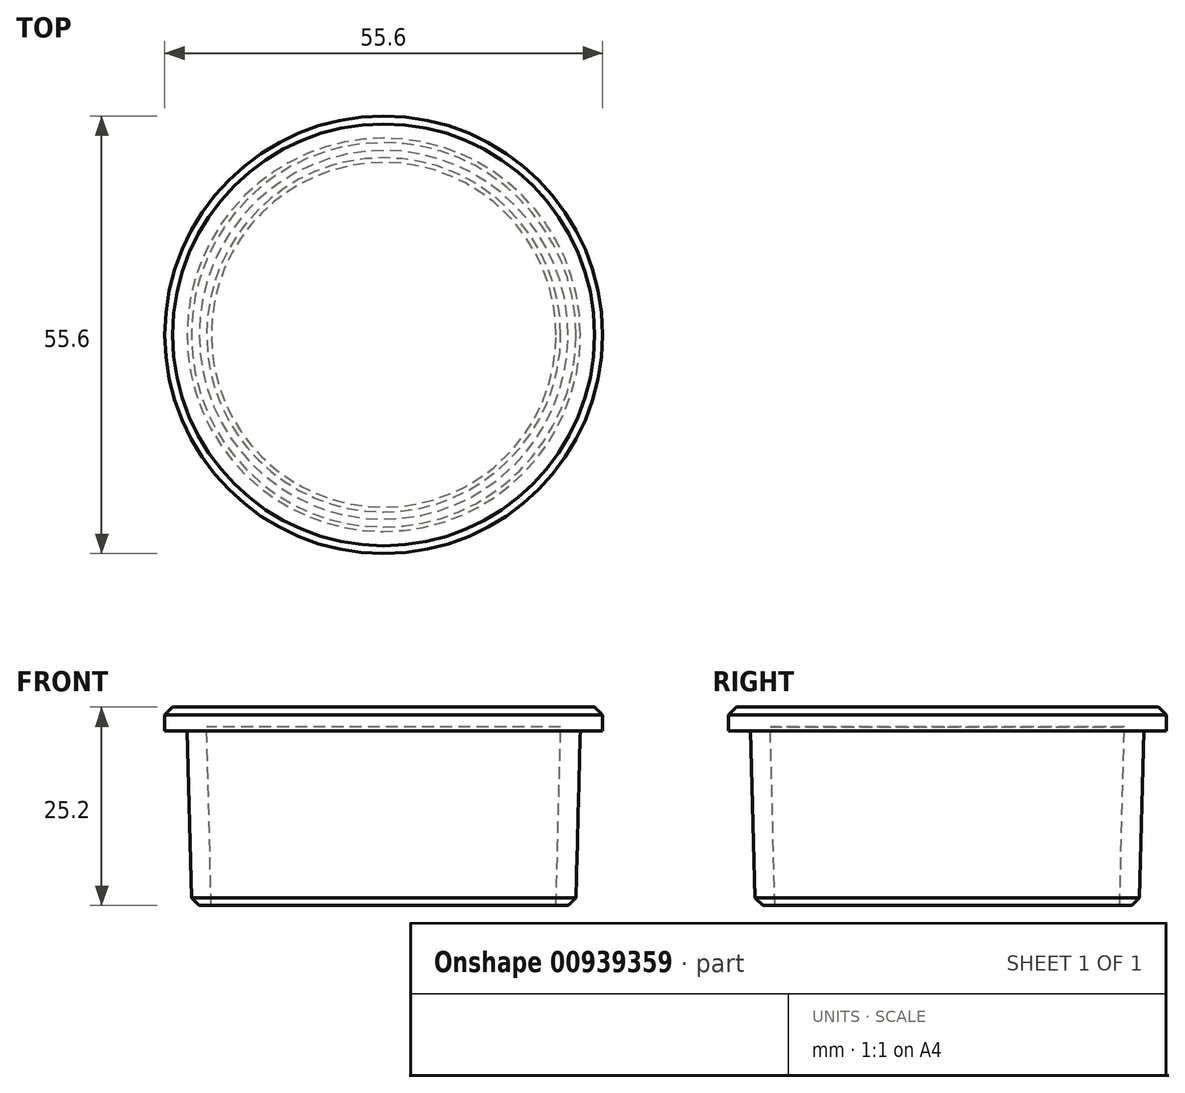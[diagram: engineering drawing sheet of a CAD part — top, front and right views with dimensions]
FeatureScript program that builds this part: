
annotation { "Feature Type Name" : "Feature", "Feature Type Description" : "" }
export const myFeature = defineFeature(function(context is Context, id is Id, definition is map)
    precondition{}
    {
        {
            var Q0;
            Q0=qCreatedBy(makeId("Top.planeOp"),FACE);
            var sketch = newSketch(context, id + "F0", { "sketchPlane" : qUnion([Q0])});
            skCircle(sketch, "E0", {"center": v(0, 0) * mm, "radius": 24.9 * mm});
            skSolve(sketch);
        }
        {
            var Q0;
            Q0 = qSketchRegion(id + "F0", true);
            extrude(context, id + "F1", {"entities" : qUnion([Q0]), "oppositeDirection" : true, "depth" : 19.2 * mm, "offsetDistance" : 25 * mm, "hasDraft" : true, "draftAngle" : 1.5 * degree, "draftPullDirection" : true, "hasSecondDirection" : true, "secondDirectionOppositeDirection" : false, "secondDirectionDepth" : 3 * mm, "hasSecondDirectionDraft" : true, "secondDirectionDraftAngle" : 1.5 * degree});
        }
        {
            var Q0;
            Q0=makeQuery(id+"F1.opExtrude","CAP_FACE",FACE,{"disambiguationData":[OSD([sQuery(id+"F0.wireOp",EDGE,"E0")])],"isStart":true});
            var sketch = newSketch(context, id + "F2", { "sketchPlane" : qUnion([Q0])});
            skCircle(sketch, "E1", {"center": v(0, 0) * mm, "radius": 27.8 * mm});
            skSolve(sketch);
        }
        {
            var Q0;
            Q0 = qSketchRegion(id + "F2", true);
            extrude(context, id + "F3", {"entities" : qUnion([Q0]), "operationType" : NewBodyOperationType.ADD, "depth" : 3 * mm, "offsetDistance" : 25 * mm});
        }
        {
            var Q0;
            Q0=makeQuery(id+"F3.opExtrude","CAP_EDGE",EDGE,{"disambiguationData":[OSD([sQuery(id+"F2.wireOp",EDGE,"E1")])],"isStart":false});
            chamfer(context, id + "F4", {"entities" : qUnion([Q0]), "width" : 1 * mm, "tangentPropagation" : true});
        }
        {
            var Q0;
            Q0=makeQuery(id+"F1.opExtrude","CAP_FACE",FACE,{"disambiguationData":[OSD([sQuery(id+"F0.wireOp",EDGE,"E0")])],"isStart":false});
            shell(context, id + "F5", {"entities" : qUnion([Q0]), "thickness" : 2.5 * mm});
        }
        {
            var Q0;
            Q0=makeQuery(id+"F1.opExtrude","CAP_EDGE",EDGE,{"disambiguationData":[OSD([sQuery(id+"F0.wireOp",EDGE,"E0")])],"isStart":false});
            chamfer(context, id + "F6", {"entities" : qUnion([Q0]), "width" : 1 * mm, "tangentPropagation" : true});
        }
    });
